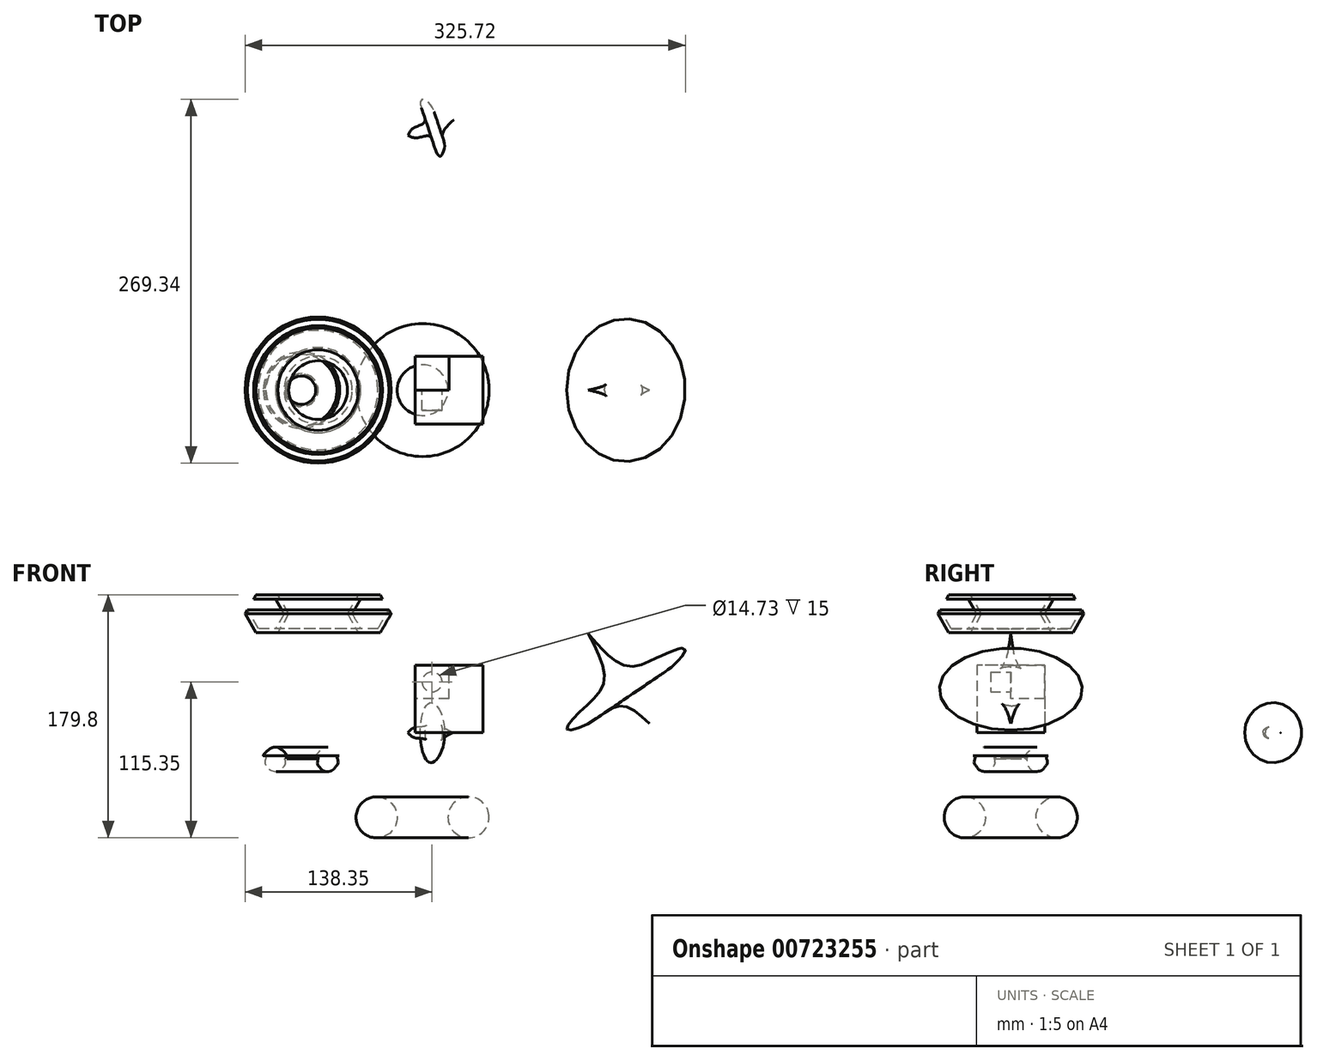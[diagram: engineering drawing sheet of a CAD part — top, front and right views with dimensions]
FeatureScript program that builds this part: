
annotation { "Feature Type Name" : "Feature", "Feature Type Description" : "" }
export const myFeature = defineFeature(function(context is Context, id is Id, definition is map)
    precondition{}
    {
        {
            var Q0;
            Q0=qCreatedBy(makeId("Top.planeOp"),FACE);
            var sketch = newSketch(context, id + "F0", { "sketchPlane" : qUnion([Q0])});
            skLineSegment(sketch, "E0.bottom", {"start": v(25, 25) * mm, "end": v(-25, 25) * mm});
            skLineSegment(sketch, "E0.top", {"start": v(25, -25) * mm, "end": v(-25, -25) * mm});
            skLineSegment(sketch, "E0.left", {"start": v(25, 25) * mm, "end": v(25, -25) * mm});
            skLineSegment(sketch, "E0.right", {"start": v(-25, 25) * mm, "end": v(-25, -25) * mm});
            skPoint(sketch, "E0.middle", {"position": v(0, 0) * mm});
            skSolve(sketch);
        }
        {
            var Q0;
            Q0=makeQuery(id+"F0.imprint","IMPRINT",FACE,{"disambiguationData":[TD([[makeQuery(id+"F0.imprint","IMPRINT",EDGE,{"derivedFrom":sQuery(id+"F0.wireOp",EDGE,"E0.bottom")}),1.0]])]});
            extrude(context, id + "F1", {"entities" : qUnion([Q0]), "depth" : 50 * mm, "offsetDistance" : 25 * mm});
        }
        {
            var Q0;
            Q0=makeQuery(id+"F1.opExtrude","CAP_FACE",FACE,{"disambiguationData":[OSD([sQuery(id+"F0.wireOp",EDGE,"E0.bottom"),sQuery(id+"F0.wireOp",EDGE,"E0.top"),sQuery(id+"F0.wireOp",EDGE,"E0.left"),sQuery(id+"F0.wireOp",EDGE,"E0.right")])],"isStart":false});
            var sketch = newSketch(context, id + "F2", { "sketchPlane" : qUnion([Q0])});
            skLineSegment(sketch, "E1.bottom", {"start": v(0, 0) * mm, "end": v(-50, 0) * mm});
            skLineSegment(sketch, "E1.top", {"start": v(0, 50) * mm, "end": v(-50, 50) * mm});
            skLineSegment(sketch, "E1.left", {"start": v(0, 0) * mm, "end": v(0, 50) * mm});
            skLineSegment(sketch, "E1.right", {"start": v(-50, 0) * mm, "end": v(-50, 50) * mm});
            skPoint(sketch, "E1.middle", {"position": v(-25, 25) * mm});
            skSolve(sketch);
        }
        {
            var Q0;
            Q0 = qSketchRegion(id + "F2", true);
            extrude(context, id + "F3", {"entities" : qUnion([Q0]), "operationType" : NewBodyOperationType.REMOVE, "oppositeDirection" : true, "depth" : 25 * mm, "offsetDistance" : 25 * mm});
        }
        {
            var Q0;
            Q0=makeQuery(id+"F3.boolean.opBoolean","COPY",FACE,{"derivedFrom":makeQuery(id+"F3.opExtrude","SWEPT_FACE",FACE,{"disambiguationData":[OSD([sQuery(id+"F2.wireOp",EDGE,"E1.bottom")])]})});
            var sketch = newSketch(context, id + "F4", { "sketchPlane" : qUnion([Q0])});
            skLineSegment(sketch, "E2", {"start": v(12.5, 50) * mm, "end": v(12.5, 25) * mm, "construction": true});
            skLineSegment(sketch, "E3", {"start": v(25, 37.5) * mm, "end": v(0, 37.5) * mm, "construction": true});
            skCircle(sketch, "E4", {"center": v(12.5, 37.5) * mm, "radius": 7.36 * mm});
            skSolve(sketch);
        }
        {
            var Q0;
            Q0=qCreatedBy(makeId("Front.planeOp"),FACE);
            var sketch = newSketch(context, id + "F5", { "sketchPlane" : qUnion([Q0])});
            skFitSpline(sketch, "E5", {"points": [v(103.04, 73.28) * mm, v(114.83, 38.16) * mm, v(98.44, 16.96) * mm, v(87.24, 2.51) * mm, v(103.9, 7.25) * mm, v(126.83, 19.84) * mm, v(148.27, 6.81) * mm], "startDerivative": vector(98.78, -187.37) * mm, "endDerivative": vector(128.72, -118.3) * mm});
            skLineSegment(sketch, "E6", {"start": v(103.04, 73.28) * mm, "end": v(148.27, 6.81) * mm});
            skSolve(sketch);
        }
        {
            var Q0;
            Q0 = qSketchRegion(id + "F5", true);
            var Q1;
            Q1=sQuery(id+"F5.wireOp",EDGE,"E6");
            revolve(context, id + "F6", {"surfaceOperationType" : NewSurfaceOperationType.NEW, "entities" : qUnion([Q0]), "axis" : qUnion([Q1]), "revolveType" : RevolveType.FULL});
        }
        {
            var Q0;
            Q0 = qSketchRegion(id + "F4", true);
            extrude(context, id + "F7", {"entities" : qUnion([Q0]), "operationType" : NewBodyOperationType.REMOVE, "oppositeDirection" : true, "depth" : 15 * mm, "offsetDistance" : 25 * mm});
        }
        {
            var Q0;
            Q0=qCreatedBy(makeId("Front.planeOp"),FACE);
            var sketch = newSketch(context, id + "F8", { "sketchPlane" : qUnion([Q0])});
            skCircle(sketch, "E7", {"center": v(-53.51, -62.65) * mm, "radius": 15.2 * mm});
            skLineSegment(sketch, "E8", {"start": v(-19.53, -44.27) * mm, "end": v(-19.53, -83.8) * mm});
            skSolve(sketch);
        }
        {
            var Q0;
            Q0 = qSketchRegion(id + "F8", true);
            var Q1;
            Q1=sQuery(id+"F8.wireOp",EDGE,"E8");
            revolve(context, id + "F9", {"surfaceOperationType" : NewSurfaceOperationType.NEW, "entities" : qUnion([Q0]), "axis" : qUnion([Q1]), "revolveType" : RevolveType.FULL});
        }
        {
            var Q0;
            Q0=qCreatedBy(makeId("Front.planeOp"),FACE);
            var sketch = newSketch(context, id + "F10", { "sketchPlane" : qUnion([Q0])});
            skFitSpline(sketch, "E9", {"points": [v(-126.76, -11.05) * mm, v(-133.22, -12.55) * mm, v(-137.3, -17.07) * mm, v(-135.58, -17.29) * mm, v(-136.23, -22.02) * mm, v(-134.5, -25.04) * mm, v(-132.36, -27.62) * mm, v(-125.68, -28.48) * mm, v(-122.67, -25.68) * mm, v(-120.95, -22.67) * mm, v(-121.38, -18.36) * mm, v(-120.09, -19.44) * mm, v(-119.87, -17.29) * mm, v(-126.76, -11.05) * mm]});
            skLineSegment(sketch, "E10", {"start": v(-109.11, -10.83) * mm, "end": v(-109.11, -27.83) * mm});
            skSolve(sketch);
        }
        {
            var Q0;
            Q0 = qSketchRegion(id + "F10", true);
            var Q1;
            Q1=sQuery(id+"F10.wireOp",EDGE,"E10");
            revolve(context, id + "F11", {"surfaceOperationType" : NewSurfaceOperationType.NEW, "entities" : qUnion([Q0]), "axis" : qUnion([Q1]), "revolveType" : RevolveType.FULL});
        }
        {
            var Q0;
            Q0=qCreatedBy(makeId("Front.planeOp"),FACE);
            var sketch = newSketch(context, id + "F12", { "sketchPlane" : qUnion([Q0])});
            skCircle(sketch, "E11.cCircle", {"center": v(-134.7, 87.96) * mm, "radius": 13.99 * mm, "construction": true});
            skLineSegment(sketch, "E11.0", {"start": v(-126.62, 73.97) * mm, "end": v(-142.77, 73.97) * mm});
            skLineSegment(sketch, "E11.1", {"start": v(-142.77, 73.97) * mm, "end": v(-150.85, 87.96) * mm});
            skLineSegment(sketch, "E11.2", {"start": v(-150.85, 87.96) * mm, "end": v(-142.77, 101.95) * mm});
            skLineSegment(sketch, "E11.3", {"start": v(-142.77, 101.95) * mm, "end": v(-126.62, 101.95) * mm});
            skLineSegment(sketch, "E11.4", {"start": v(-126.62, 101.95) * mm, "end": v(-118.54, 87.96) * mm});
            skLineSegment(sketch, "E11.5", {"start": v(-118.54, 87.96) * mm, "end": v(-126.62, 73.97) * mm});
            skPoint(sketch, "E11.0.midPoint", {"position": v(-134.7, 73.97) * mm});
            skLineSegment(sketch, "E12", {"start": v(-96.82, 101.95) * mm, "end": v(-96.82, 72.03) * mm});
            skSolve(sketch);
        }
        {
            var Q0;
            Q0 = qSketchRegion(id + "F12", true);
            var Q1;
            Q1=sQuery(id+"F12.wireOp",EDGE,"E12");
            revolve(context, id + "F13", {"surfaceOperationType" : NewSurfaceOperationType.NEW, "entities" : qUnion([Q0]), "axis" : qUnion([Q1]), "revolveType" : RevolveType.FULL});
        }
        {
            var Q0;
            Q0=makeQuery(id+"F13.opRevolve","SWEPT_FACE",FACE,{"disambiguationData":[OSD([sQuery(id+"F12.wireOp",EDGE,"E11.2")])]});
            shell(context, id + "F14", {"entities" : qUnion([Q0]), "thickness" : 3 * mm});
        }
        {
            var Q0;
            Q0=qCreatedBy(makeId("Top.planeOp"),FACE);
            var sketch = newSketch(context, id + "F15", { "sketchPlane" : qUnion([Q0])});
            skLineSegment(sketch, "E13", {"start": v(-49.81, 182.02) * mm, "end": v(24.31, 206.68) * mm, "construction": true});
            skFitSpline(sketch, "E14", {"points": [v(-30.48, 188.45) * mm, v(-23.85, 186.65) * mm, v(-14.47, 187.88) * mm, v(-10.23, 178.38) * mm, v(-6.32, 173.08) * mm, v(-3.31, 182.02) * mm, v(-4.6, 190.4) * mm, v(3.19, 199.66) * mm, v(3.51, 199.76) * mm], "startDerivative": vector(49.15, -25.19) * mm, "endDerivative": vector(7.4, -0.48) * mm});
            skLineSegment(sketch, "E15", {"start": v(-30.48, 188.45) * mm, "end": v(3.51, 199.76) * mm});
            skSolve(sketch);
        }
        {
            var Q0;
            Q0 = qSketchRegion(id + "F15", true);
            var Q1;
            Q1=sQuery(id+"F15.wireOp",EDGE,"E15");
            revolve(context, id + "F16", {"surfaceOperationType" : NewSurfaceOperationType.NEW, "entities" : qUnion([Q0]), "axis" : qUnion([Q1]), "revolveType" : RevolveType.FULL});
        }
    });
